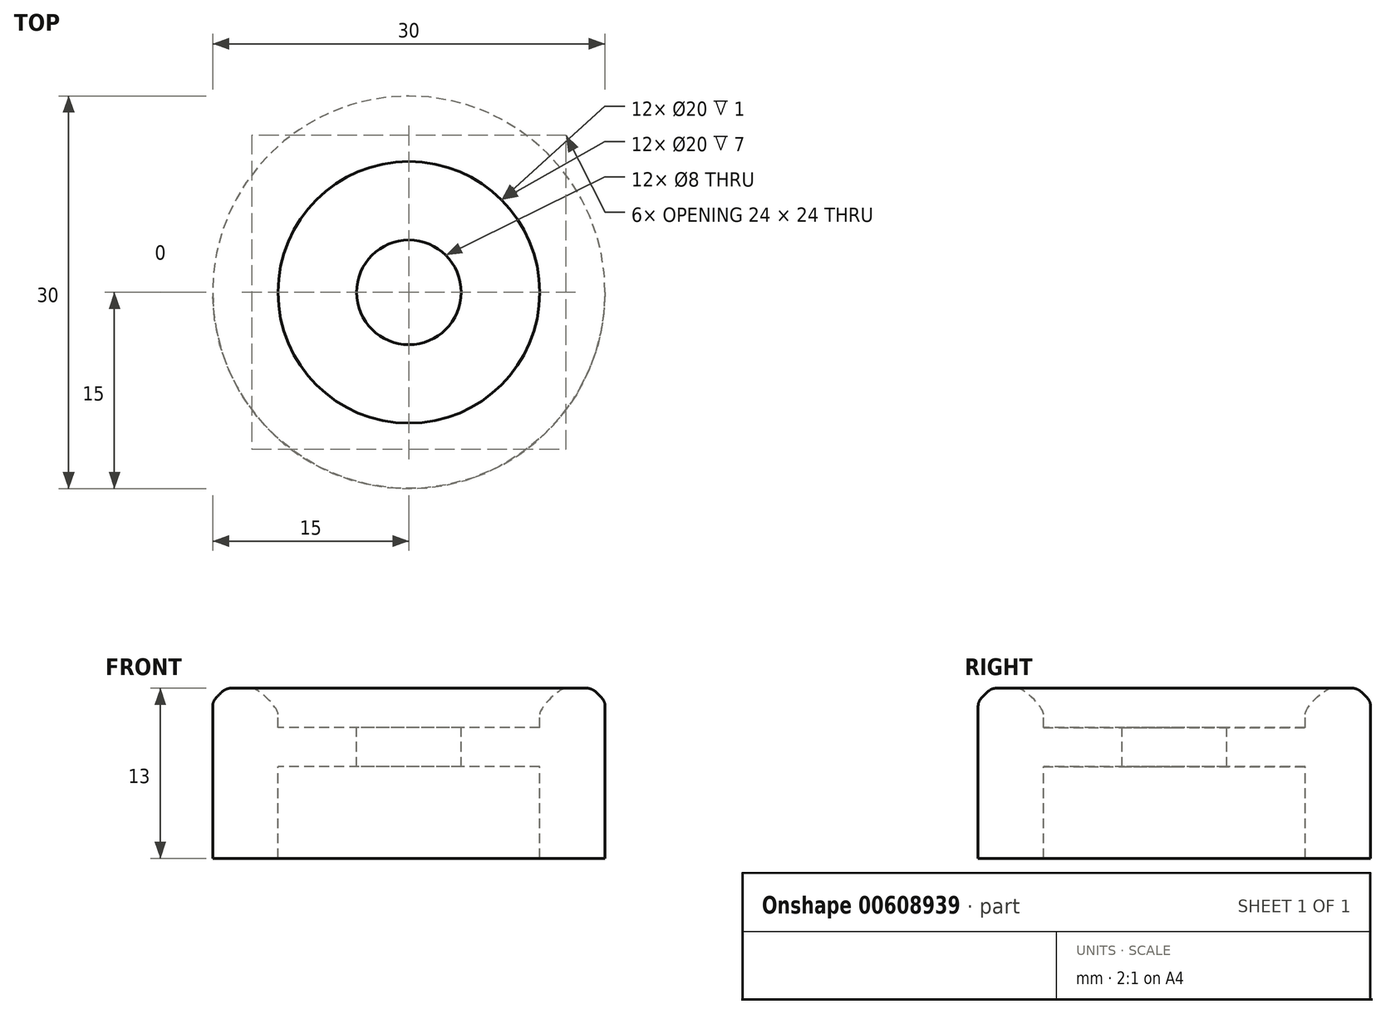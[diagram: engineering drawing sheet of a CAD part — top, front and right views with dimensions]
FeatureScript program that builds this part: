
annotation { "Feature Type Name" : "Feature", "Feature Type Description" : "" }
export const myFeature = defineFeature(function(context is Context, id is Id, definition is map)
    precondition{}
    {
        {
            var Q0;
            Q0=qCreatedBy(makeId("Front.planeOp"),FACE);
            var sketch = newSketch(context, id + "F0", { "sketchPlane" : qUnion([Q0])});
            skLineSegment(sketch, "E0", {"start": v(0, 0) * mm, "end": v(-10, 0) * mm});
            skLineSegment(sketch, "E1", {"start": v(-10, 0) * mm, "end": v(-10, -7) * mm});
            skLineSegment(sketch, "E2", {"start": v(-10, -7) * mm, "end": v(-15, -7) * mm});
            skLineSegment(sketch, "E3", {"start": v(-15, -7) * mm, "end": v(-15, 6) * mm});
            skLineSegment(sketch, "E4", {"start": v(-15, 6) * mm, "end": v(-10, 6) * mm});
            skLineSegment(sketch, "E5", {"start": v(-10, 6) * mm, "end": v(-10, 3) * mm});
            skLineSegment(sketch, "E6", {"start": v(-10, 3) * mm, "end": v(0, 3) * mm});
            skLineSegment(sketch, "E7", {"start": v(0, 3) * mm, "end": v(0, 0) * mm});
            skSolve(sketch);
        }
        {
            var Q0;
            Q0 = qSketchRegion(id + "F0", true);
            var Q1;
            Q1=sQuery(id+"F0.wireOp",EDGE,"E7");
            revolve(context, id + "F1", {"entities" : qUnion([Q0]), "axis" : qUnion([Q1]), "revolveType" : RevolveType.FULL});
        }
        {
            var Q0;
            Q0=makeQuery(id+"F1.opRevolve","SWEPT_FACE",FACE,{"disambiguationData":[OSD([sQuery(id+"F0.wireOp",EDGE,"E6")])]});
            var sketch = newSketch(context, id + "F2", { "sketchPlane" : qUnion([Q0])});
            skCircle(sketch, "E8", {"center": v(0, 0) * mm, "radius": 4 * mm});
            skSolve(sketch);
        }
        {
            var Q0;
            Q0=makeQuery(id+"F2.imprint","IMPRINT",FACE,{"disambiguationData":[TD([[makeQuery(id+"F2.imprint","IMPRINT",EDGE,{"derivedFrom":sQuery(id+"F2.wireOp",EDGE,"E8")}),1.0]])]});
            extrude(context, id + "F3", {"entities" : qUnion([Q0]), "operationType" : NewBodyOperationType.REMOVE, "oppositeDirection" : true, "depth" : 25 * mm, "offsetDistance" : 25 * mm});
        }
        {
            var Q0;
            Q0=makeQuery(id+"F1.opRevolve","SWEPT_EDGE",EDGE,{"disambiguationData":[OSD([sQuery(id+"F0.wireOp",EDGE,"E4"),sQuery(id+"F0.wireOp",EDGE,"E5")])]});
            fillet(context, id + "F4", {"entities" : qUnion([Q0]), "radius" : 2 * mm, "rho" : .2, "crossSection" : FilletCrossSection.CONIC, "allowEdgeOverflow" : false});
        }
        {
            var Q0;
            Q0=makeQuery(id+"F1.opRevolve","SWEPT_EDGE",EDGE,{"disambiguationData":[OSD([sQuery(id+"F0.wireOp",EDGE,"E3"),sQuery(id+"F0.wireOp",EDGE,"E4")])]});
            chamfer(context, id + "F5", {"entities" : qUnion([Q0]), "width" : 1 * mm, "tangentPropagation" : true});
        }
        {
            var Q0;
            {var subQ0=sQuery(id+"F0.wireOp",EDGE,"E4");Q0=makeQuery(id+"F5.opChamfer","BLEND_EDGE",EDGE,{"blendedFrom":[makeQuery(id+"F1.opRevolve","SWEPT_EDGE",EDGE,{"disambiguationData":[OSD([sQuery(id+"F0.wireOp",EDGE,"E3"),subQ0])]}),makeQuery(id+"F1.opRevolve","SWEPT_FACE",FACE,{"disambiguationData":[OSD([subQ0])]})],"blendedInto":[makeQuery(id+"F1.opRevolve","SWEPT_FACE",FACE,{"disambiguationData":[OSD([subQ0])]})]});}
            fillet(context, id + "F6", {"entities" : qUnion([Q0]), "radius" : 1 * mm, "tangentPropagation" : true, "allowEdgeOverflow" : false});
        }
        {
            var Q0;
            {var subQ0=sQuery(id+"F0.wireOp",EDGE,"E3");Q0=makeQuery(id+"F5.opChamfer","BLEND_EDGE",EDGE,{"blendedFrom":[makeQuery(id+"F1.opRevolve","SWEPT_EDGE",EDGE,{"disambiguationData":[OSD([subQ0,sQuery(id+"F0.wireOp",EDGE,"E4")])]}),makeQuery(id+"F1.opRevolve","SWEPT_FACE",FACE,{"disambiguationData":[OSD([subQ0])]})],"blendedInto":[makeQuery(id+"F1.opRevolve","SWEPT_FACE",FACE,{"disambiguationData":[OSD([subQ0])]})]});}
            fillet(context, id + "F7", {"entities" : qUnion([Q0]), "radius" : 1 * mm, "rho" : 0.5, "crossSection" : FilletCrossSection.CONIC, "allowEdgeOverflow" : false});
        }
    });
